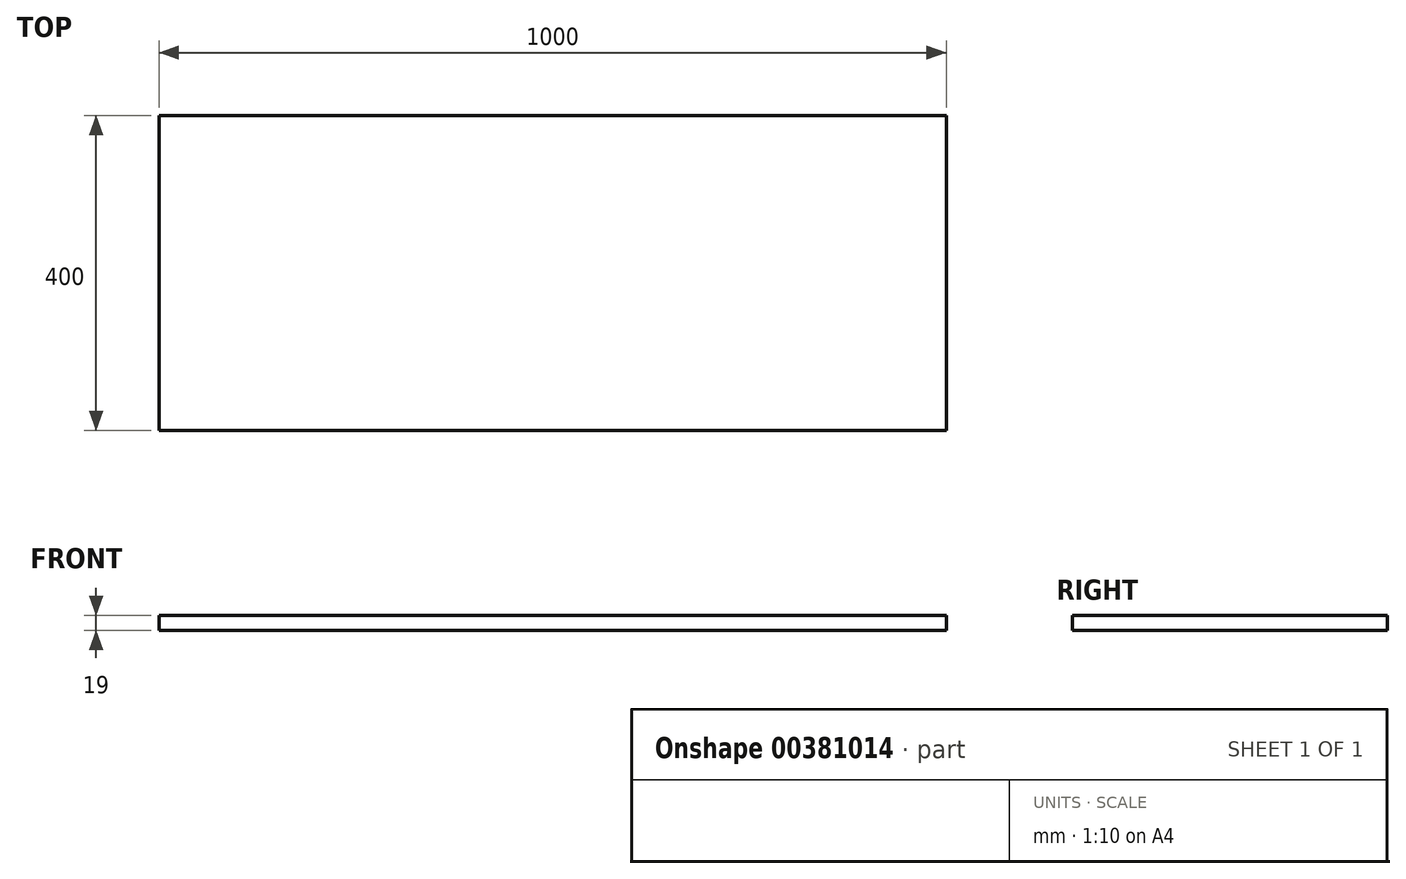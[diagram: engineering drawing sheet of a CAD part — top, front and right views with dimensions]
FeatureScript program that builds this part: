
annotation { "Feature Type Name" : "Feature", "Feature Type Description" : "" }
export const myFeature = defineFeature(function(context is Context, id is Id, definition is map)
    precondition{}
    {
        {
            var Q0;
            Q0=qCreatedBy(makeId("Top.planeOp"),FACE);
            var sketch = newSketch(context, id + "F0", { "sketchPlane" : qUnion([Q0])});
            skLineSegment(sketch, "E0.bottom", {"start": v(500, -200) * mm, "end": v(-500, -200) * mm});
            skLineSegment(sketch, "E0.top", {"start": v(500, 200) * mm, "end": v(-500, 200) * mm});
            skLineSegment(sketch, "E0.left", {"start": v(500, -200) * mm, "end": v(500, 200) * mm});
            skLineSegment(sketch, "E0.right", {"start": v(-500, -200) * mm, "end": v(-500, 200) * mm});
            skPoint(sketch, "E0.middle", {"position": v(0, 0) * mm});
            skSolve(sketch);
        }
        {
            var Q0;
            Q0=makeQuery(id+"F0.imprint","IMPRINT",FACE,{"disambiguationData":[TD([[makeQuery(id+"F0.imprint","IMPRINT",EDGE,{"derivedFrom":sQuery(id+"F0.wireOp",EDGE,"E0.bottom")}),-1.0]])]});
            extrude(context, id + "F1", {"entities" : qUnion([Q0]), "depth" : 19 * mm});
        }
    });
